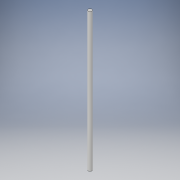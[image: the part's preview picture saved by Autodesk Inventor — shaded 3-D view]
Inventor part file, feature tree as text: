
AUTODESK INVENTOR PART (.ipt)
format: ipt  version: 2019 (Build 230136000, 136)  size: 89,088 bytes
history: native  units: mm
features: extrude x1, sketch x1
ambient origin geometry x8: Origin, YZ Plane, XZ Plane, XY Plane, X Axis, Y Axis, Z Axis, Center Point
bodies: Solid1 (feature_tree)
feature tree (2):
  extrude  "Extrusion1"  Depth=560.0mm TaperAngle=0.0deg
  sketch  "Sketch1"  dims[d0=15.0mm d1=560.0mm d2=0.0mm]
